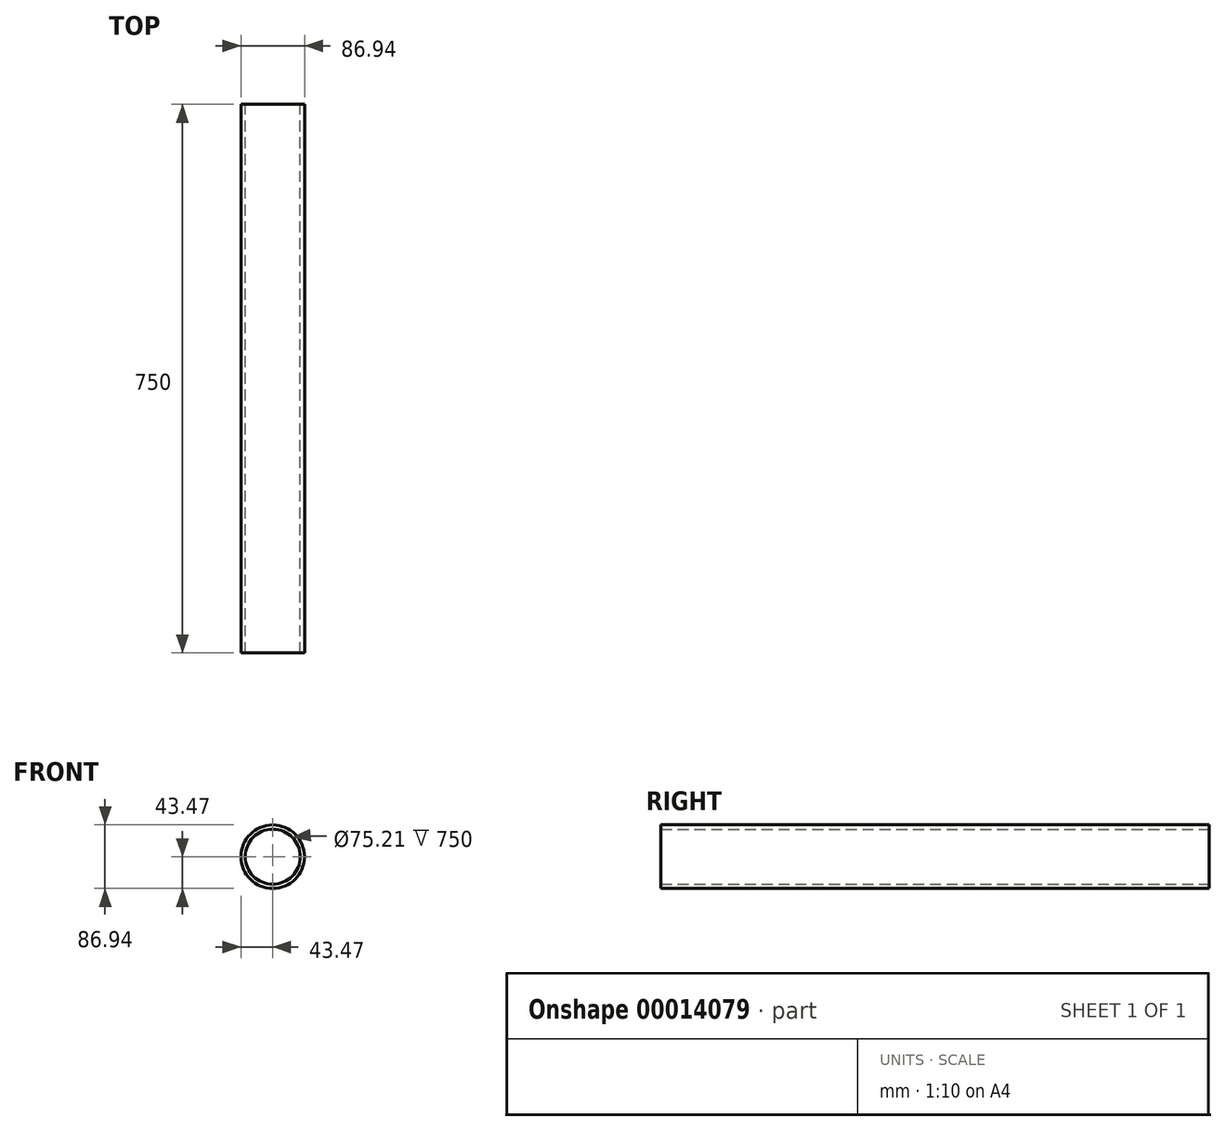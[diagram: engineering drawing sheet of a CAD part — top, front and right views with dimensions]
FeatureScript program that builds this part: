
annotation { "Feature Type Name" : "Feature", "Feature Type Description" : "" }
export const myFeature = defineFeature(function(context is Context, id is Id, definition is map)
    precondition{}
    {
        {
            var Q0;
            Q0=qCreatedBy(makeId("Front.planeOp"),FACE);
            var sketch = newSketch(context, id + "F0", { "sketchPlane" : qUnion([Q0])});
            skCircle(sketch, "E0", {"center": v(0, 0) * mm, "radius": 43.47 * mm});
            skLineSegment(sketch, "E1", {"start": v(0, 0) * mm, "end": v(0, 43.47) * mm, "construction": true});
            skCircle(sketch, "E2", {"center": v(0, 0) * mm, "radius": 37.6 * mm});
            skSolve(sketch);
        }
        {
            var Q0;
            Q0=makeQuery(id+"F0.imprint","IMPRINT",FACE,{"disambiguationData":[TD([[makeQuery(id+"F0.imprint","IMPRINT",EDGE,{"derivedFrom":sQuery(id+"F0.wireOp",EDGE,"E0")}),1.0]])]});
            var Q1;
            Q1=sQuery(id+"F0.wireOp",EDGE,"E0");
            var Q2;
            Q2=sQuery(id+"F0.wireOp",EDGE,"E2");
            extrude(context, id + "F1", {"entities" : qUnion([Q0]), "surfaceEntities" : qUnion([Q1, Q2]), "depth" : 750 * mm, "symmetric" : true});
        }
    });
